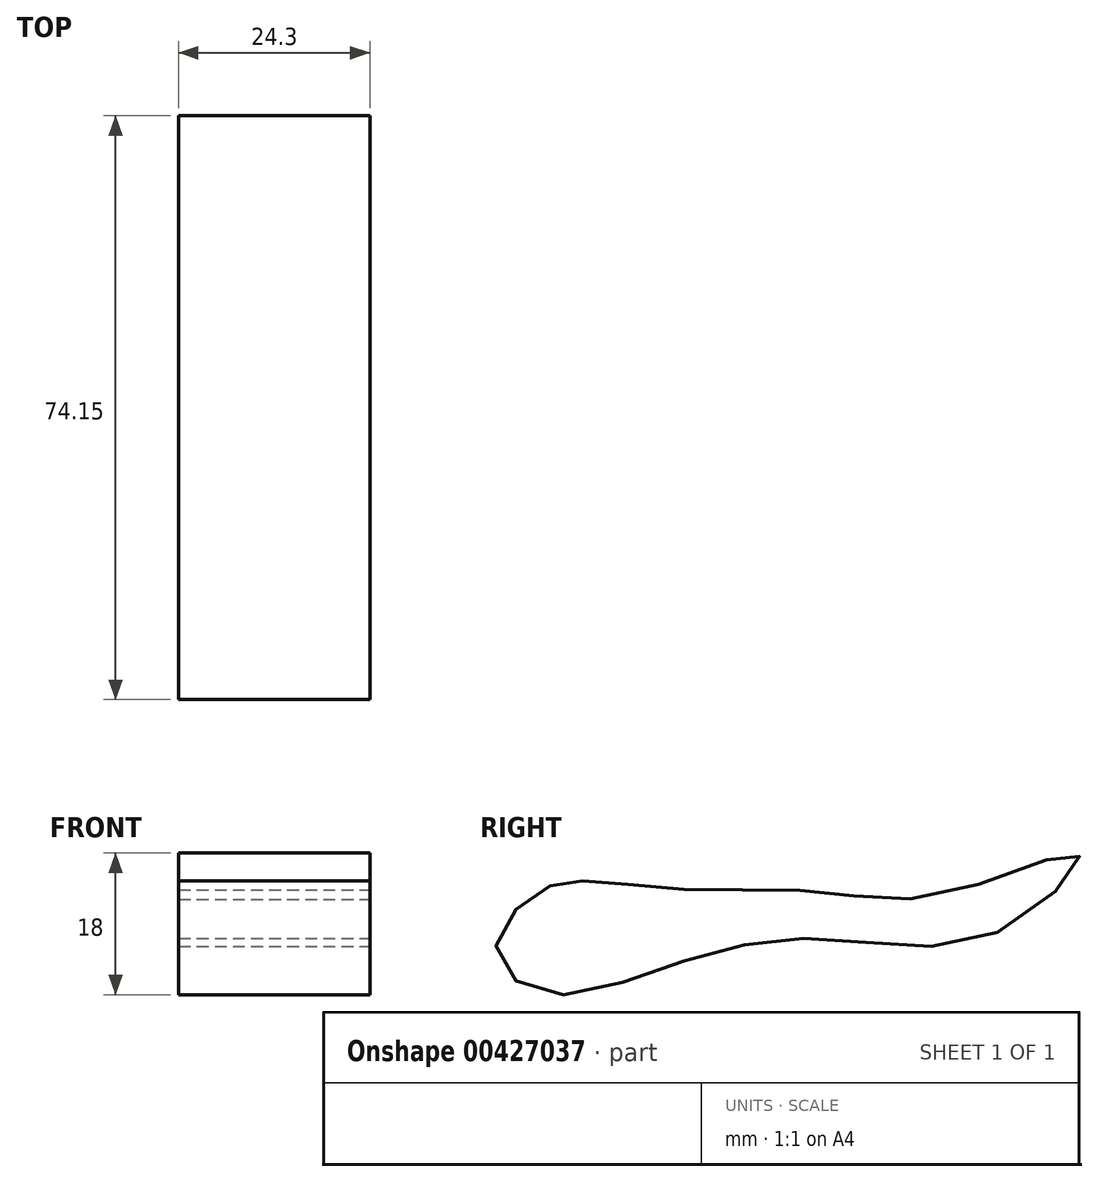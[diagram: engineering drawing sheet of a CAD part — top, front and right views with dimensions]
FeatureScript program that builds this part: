
annotation { "Feature Type Name" : "Feature", "Feature Type Description" : "" }
export const myFeature = defineFeature(function(context is Context, id is Id, definition is map)
    precondition{}
    {
        {
            var Q0;
            Q0=qCreatedBy(makeId("Right.planeOp"),FACE);
            var sketch = newSketch(context, id + "F0", { "sketchPlane" : qUnion([Q0])});
            skFitSpline(sketch, "E0", {"points": [v(-65.47, 0) * mm, v(-64.5, 4.03) * mm, v(-60.34, 8.43) * mm, v(-52.28, 9.4) * mm, v(-38.36, 9.9) * mm, v(-19.54, 6.47) * mm, v(-9.77, 5.25) * mm, v(8.06, 7.7) * mm, v(20.28, 13.07) * mm, v(28.58, 20.4) * mm, v(24.43, 6.96) * mm, v(15.15, -3.79) * mm, v(-3.42, -9.16) * mm, v(-22.23, -9.4) * mm, v(-43.73, -7.94) * mm, v(-60.83, -4.52) * mm, v(-65.47, 0) * mm]});
            skSolve(sketch);
        }
        {
            var Q0;
            Q0 = qConstructionFilter(qBodyType(qCreatedBy(id + "F0" ,EDGE), BodyType.WIRE), ConstructionObject.NO);
            extrude(context, id + "F1", {"bodyType" : ToolBodyType.SURFACE, "surfaceEntities" : qUnion([Q0]), "oppositeDirection" : true, "depth" : 92.2 * mm});
        }
        {
            var Q0;
            Q0=qCreatedBy(makeId("Right.planeOp"),FACE);
            cPlane(context, id + "F2", {"entities" : qUnion([Q0]), "cplaneType" : CPlaneType.OFFSET, "offset" : 106.4 * mm, "oppositeDirection" : true, "width" : 152.4 * mm, "height" : 152.4 * mm});
        }
        {
            var Q0;
            Q0=qCreatedBy(id+"F2.planeOp",FACE);
            var sketch = newSketch(context, id + "F3", { "sketchPlane" : qUnion([Q0])});
            skFitSpline(sketch, "E1", {"points": [v(-26.87, -33.32) * mm, v(-39.76, -32.22) * mm, v(-45.25, -33.6) * mm, v(-50.73, -40.45) * mm, v(-44.7, -46.48) * mm, v(-26.6, -42.37) * mm, v(-8.5, -39.63) * mm, v(12.89, -38.8) * mm, v(23.3, -28.93) * mm, v(6.58, -33.87) * mm, v(-10.15, -33.6) * mm, v(-26.87, -33.32) * mm]});
            skSolve(sketch);
        }
        {
            var Q0;
            Q0=makeQuery(id+"F3.imprint","IMPRINT",FACE,{"disambiguationData":[TD([[makeQuery(id+"F3.imprint","IMPRINT",EDGE,{"derivedFrom":sQuery(id+"F3.wireOp",EDGE,"E1")}),1.0]])]});
            extrude(context, id + "F4", {"entities" : qUnion([Q0]), "oppositeDirection" : true, "depth" : 24.3 * mm});
        }
        {
            var Q0;
            Q0=makeQuery(id+"F4.opExtrude","SWEPT_BODY",BODY,{"disambiguationData":[OSD([sQuery(id+"F3.wireOp",EDGE,"E1")])]});
            var Q1;
            Q1=qCreatedBy(makeId("Top.planeOp"),FACE);
            transform(context, id + "F5", {"entities" : qUnion([Q0]), "transformType" : TransformType.TRANSLATION_DISTANCE, "transformDirection" : qUnion([Q1]), "distance" : 37.8 * mm, "makeCopy" : false});
        }
        {
            var Q0;
            Q0=makeQuery(id+"F3.imprint","IMPRINT",FACE,{"disambiguationData":[TD([[makeQuery(id+"F3.imprint","IMPRINT",EDGE,{"derivedFrom":sQuery(id+"F3.wireOp",EDGE,"E1")}),1.0]])]});
            var Q1;
            Q1=makeQuery(id+"F0.imprint","IMPRINT",FACE,{"disambiguationData":[TD([[makeQuery(id+"F0.imprint","IMPRINT",EDGE,{"derivedFrom":sQuery(id+"F0.wireOp",EDGE,"E0")}),-1.0]])]});
            var Q2;
            Q2=makeQuery(id+"F1.opExtrude","CAP_EDGE",EDGE,{"disambiguationData":[OSD([sQuery(id+"F0.wireOp",EDGE,"E0")])],"isStart":false});
            var Q3;
            Q3=makeQuery(id+"F4.opExtrude","CAP_EDGE",EDGE,{"disambiguationData":[OSD([sQuery(id+"F3.wireOp",EDGE,"E1")])],"isStart":true});
            loft(context, id + "F6", {"bodyType" : ToolBodyType.SURFACE, "sheetProfilesArray" : [{ "sheetProfileEntities" : qUnion([Q0]) }, { "sheetProfileEntities" : qUnion([Q1]) }], "wireProfilesArray" : [{ "wireProfileEntities" : qUnion([Q2]) }, { "wireProfileEntities" : qUnion([Q3]) }]});
        }
    });
